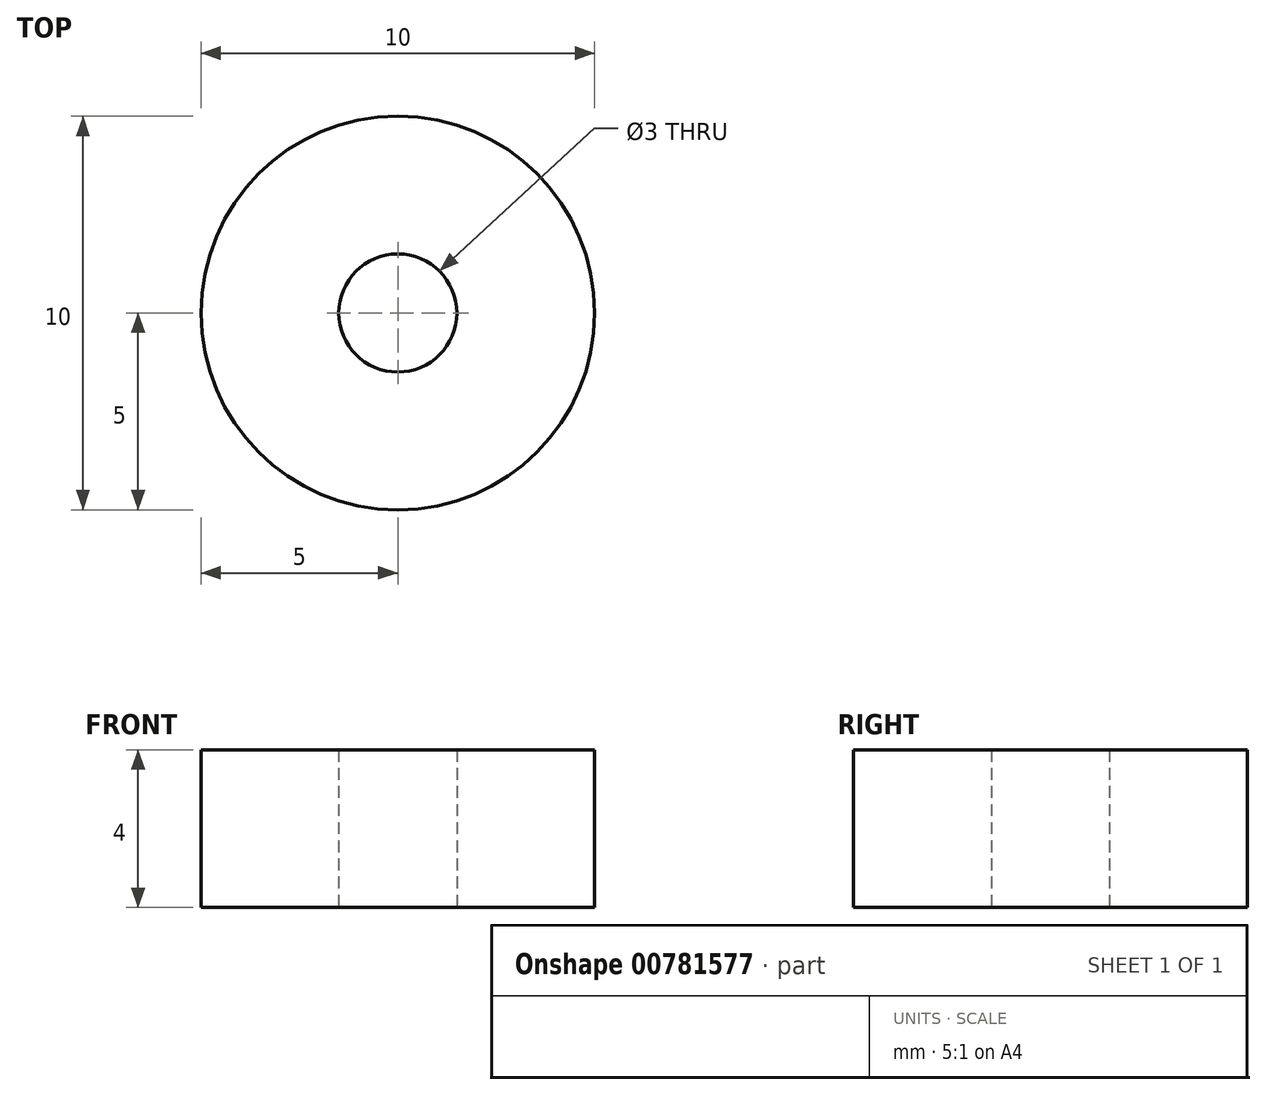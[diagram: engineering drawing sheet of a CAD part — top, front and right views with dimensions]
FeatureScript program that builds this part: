
annotation { "Feature Type Name" : "Feature", "Feature Type Description" : "" }
export const myFeature = defineFeature(function(context is Context, id is Id, definition is map)
    precondition{}
    {
        {
            var Q0;
            Q0=qCreatedBy(makeId("Top.planeOp"),FACE);
            var sketch = newSketch(context, id + "F0", { "sketchPlane" : qUnion([Q0])});
            skCircle(sketch, "E0", {"center": v(0, 0) * mm, "radius": 5 * mm});
            skCircle(sketch, "E1", {"center": v(0, 0) * mm, "radius": 1.5 * mm});
            skSolve(sketch);
        }
        {
            var Q0;
            Q0 = qSketchRegion(id + "F0", true);
            extrude(context, id + "F1", {"entities" : qUnion([Q0]), "endBound" : BoundingType.SYMMETRIC, "depth" : 4 * mm, "offsetDistance" : 25 * mm});
        }
    });
